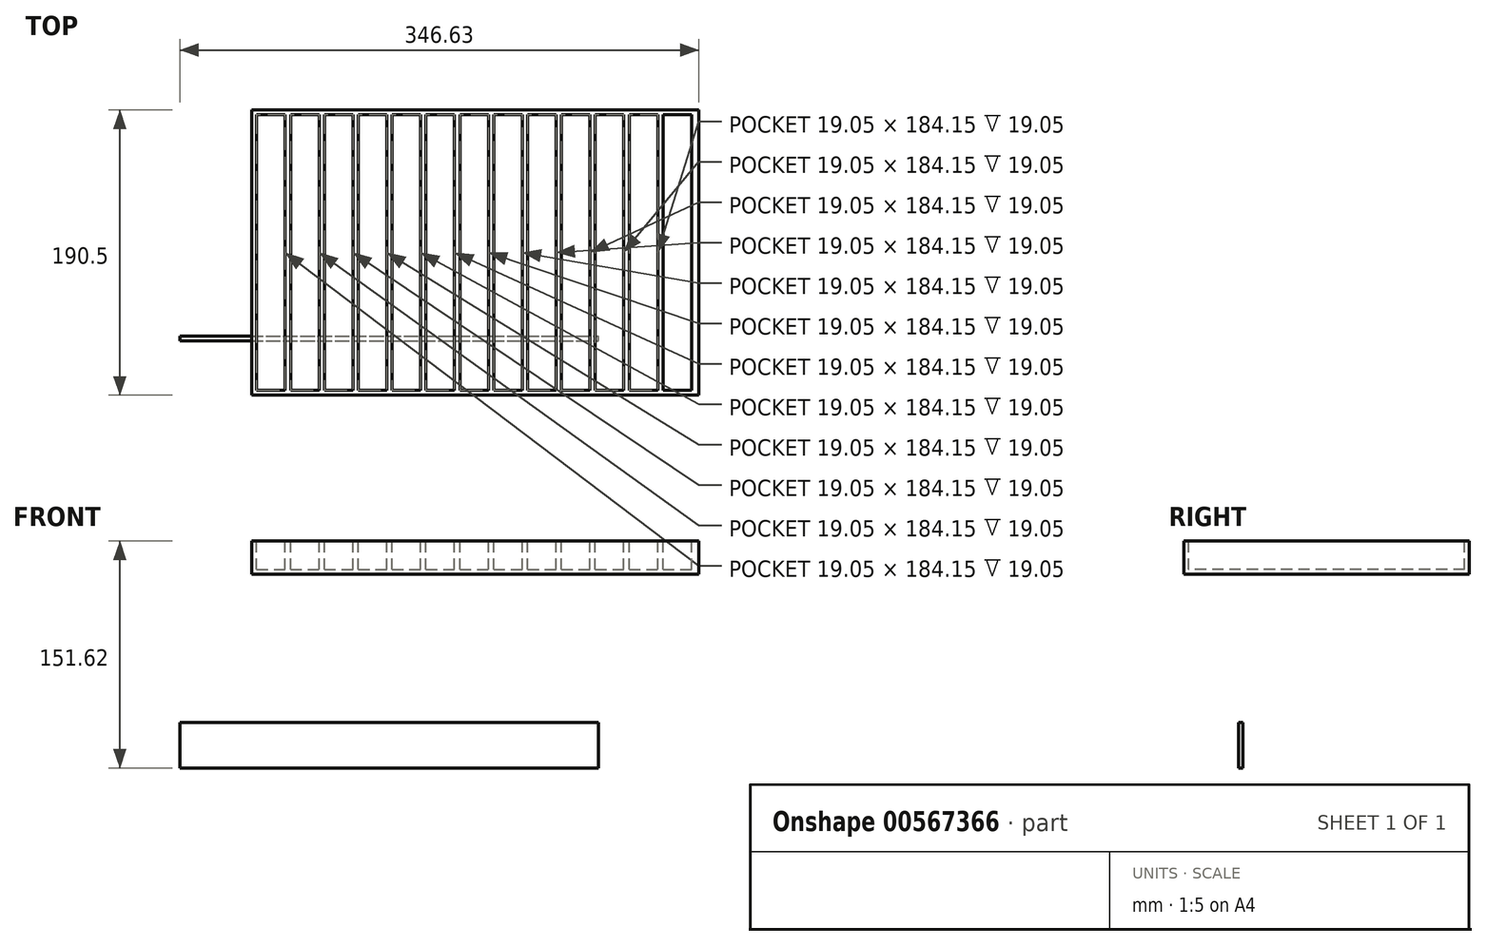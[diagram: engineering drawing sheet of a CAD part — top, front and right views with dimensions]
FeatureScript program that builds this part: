
annotation { "Feature Type Name" : "Feature", "Feature Type Description" : "" }
export const myFeature = defineFeature(function(context is Context, id is Id, definition is map)
    precondition{}
    {
        {
            var Q0;
            Q0=qCreatedBy(makeId("Top.planeOp"),FACE);
            var sketch = newSketch(context, id + "F0", { "sketchPlane" : qUnion([Q0])});
            skLineSegment(sketch, "E0.bottom", {"start": v(-114.24, 151.05) * mm, "end": v(184.2, 151.05) * mm});
            skLineSegment(sketch, "E0.top", {"start": v(-114.24, -39.45) * mm, "end": v(184.2, -39.45) * mm});
            skLineSegment(sketch, "E0.left", {"start": v(-114.24, 151.05) * mm, "end": v(-114.24, -39.45) * mm});
            skLineSegment(sketch, "E0.right", {"start": v(184.2, 151.05) * mm, "end": v(184.2, -39.45) * mm});
            skSolve(sketch);
        }
        {
            var Q0;
            Q0=makeQuery(id+"F0.imprint","IMPRINT",FACE,{"disambiguationData":[TD([[makeQuery(id+"F0.imprint","IMPRINT",EDGE,{"derivedFrom":sQuery(id+"F0.wireOp",EDGE,"E0.bottom")}),-1.0]])]});
            extrude(context, id + "F1", {"entities" : qUnion([Q0]), "depth" : 22.22 * mm, "offsetDistance" : 25.4 * mm});
        }
        {
            var Q0;
            Q0=qCreatedBy(makeId("Front.planeOp"),FACE);
            var sketch = newSketch(context, id + "F2", { "sketchPlane" : qUnion([Q0])});
            skLineSegment(sketch, "E1.bottom", {"start": v(-162.42, -98.91) * mm, "end": v(116.98, -98.91) * mm});
            skLineSegment(sketch, "E1.top", {"start": v(-162.42, -129.4) * mm, "end": v(116.98, -129.4) * mm});
            skLineSegment(sketch, "E1.left", {"start": v(-162.42, -98.91) * mm, "end": v(-162.42, -129.4) * mm});
            skLineSegment(sketch, "E1.right", {"start": v(116.98, -98.91) * mm, "end": v(116.98, -129.4) * mm});
            skSolve(sketch);
        }
        {
            var Q0;
            Q0=makeQuery(id+"F2.imprint","IMPRINT",FACE,{"disambiguationData":[TD([[makeQuery(id+"F2.imprint","IMPRINT",EDGE,{"derivedFrom":sQuery(id+"F2.wireOp",EDGE,"E1.bottom")}),-1.0]])]});
            extrude(context, id + "F3", {"entities" : qUnion([Q0]), "depth" : 3.17 * mm, "offsetDistance" : 25.4 * mm});
        }
        {
            var Q0;
            Q0=makeQuery(id+"F1.opExtrude","CAP_FACE",FACE,{"disambiguationData":[OSD([sQuery(id+"F0.wireOp",EDGE,"E0.bottom"),sQuery(id+"F0.wireOp",EDGE,"E0.top"),sQuery(id+"F0.wireOp",EDGE,"E0.left"),sQuery(id+"F0.wireOp",EDGE,"E0.right")])],"isStart":false});
            var sketch = newSketch(context, id + "F4", { "sketchPlane" : qUnion([Q0])});
            skLineSegment(sketch, "E2.bottom", {"start": v(-111.07, 147.87) * mm, "end": v(-92.02, 147.87) * mm});
            skLineSegment(sketch, "E2.top", {"start": v(-111.07, -36.28) * mm, "end": v(-92.02, -36.28) * mm});
            skLineSegment(sketch, "E2.left", {"start": v(-111.07, 147.87) * mm, "end": v(-111.07, -36.28) * mm});
            skLineSegment(sketch, "E2.right", {"start": v(-92.02, 147.87) * mm, "end": v(-92.02, -36.28) * mm});
            skLineSegment(sketch, "E3.1.0.0", {"start": v(-88.46, 147.87) * mm, "end": v(-88.46, -36.28) * mm});
            skLineSegment(sketch, "E3.1.0.1", {"start": v(-69.41, 147.87) * mm, "end": v(-69.41, -36.28) * mm});
            skLineSegment(sketch, "E3.1.0.2", {"start": v(-88.46, 147.87) * mm, "end": v(-69.41, 147.87) * mm});
            skLineSegment(sketch, "E3.1.0.3", {"start": v(-88.46, -36.28) * mm, "end": v(-69.41, -36.28) * mm});
            skLineSegment(sketch, "E3.2.0.0", {"start": v(-65.86, 147.87) * mm, "end": v(-65.86, -36.28) * mm});
            skLineSegment(sketch, "E3.2.0.1", {"start": v(-46.8, 147.87) * mm, "end": v(-46.8, -36.28) * mm});
            skLineSegment(sketch, "E3.2.0.2", {"start": v(-65.86, 147.87) * mm, "end": v(-46.8, 147.87) * mm});
            skLineSegment(sketch, "E3.2.0.3", {"start": v(-65.86, -36.28) * mm, "end": v(-46.8, -36.28) * mm});
            skLineSegment(sketch, "E3.3.0.0", {"start": v(-43.25, 147.87) * mm, "end": v(-43.25, -36.28) * mm});
            skLineSegment(sketch, "E3.3.0.1", {"start": v(-24.2, 147.87) * mm, "end": v(-24.2, -36.28) * mm});
            skLineSegment(sketch, "E3.3.0.2", {"start": v(-43.25, 147.87) * mm, "end": v(-24.2, 147.87) * mm});
            skLineSegment(sketch, "E3.3.0.3", {"start": v(-43.25, -36.28) * mm, "end": v(-24.2, -36.28) * mm});
            skLineSegment(sketch, "E3.4.0.0", {"start": v(-20.65, 147.87) * mm, "end": v(-20.65, -36.28) * mm});
            skLineSegment(sketch, "E3.4.0.1", {"start": v(-1.6, 147.87) * mm, "end": v(-1.6, -36.28) * mm});
            skLineSegment(sketch, "E3.4.0.2", {"start": v(-20.65, 147.87) * mm, "end": v(-1.6, 147.87) * mm});
            skLineSegment(sketch, "E3.4.0.3", {"start": v(-20.65, -36.28) * mm, "end": v(-1.6, -36.28) * mm});
            skLineSegment(sketch, "E3.5.0.0", {"start": v(1.96, 147.87) * mm, "end": v(1.96, -36.28) * mm});
            skLineSegment(sketch, "E3.5.0.1", {"start": v(21.01, 147.87) * mm, "end": v(21.01, -36.28) * mm});
            skLineSegment(sketch, "E3.5.0.2", {"start": v(1.96, 147.87) * mm, "end": v(21.01, 147.87) * mm});
            skLineSegment(sketch, "E3.5.0.3", {"start": v(1.96, -36.28) * mm, "end": v(21.01, -36.28) * mm});
            skLineSegment(sketch, "E3.6.0.0", {"start": v(24.57, 147.87) * mm, "end": v(24.57, -36.28) * mm});
            skLineSegment(sketch, "E3.6.0.1", {"start": v(43.62, 147.87) * mm, "end": v(43.62, -36.28) * mm});
            skLineSegment(sketch, "E3.6.0.2", {"start": v(24.57, 147.87) * mm, "end": v(43.62, 147.87) * mm});
            skLineSegment(sketch, "E3.6.0.3", {"start": v(24.57, -36.28) * mm, "end": v(43.62, -36.28) * mm});
            skLineSegment(sketch, "E3.7.0.0", {"start": v(47.17, 147.87) * mm, "end": v(47.17, -36.28) * mm});
            skLineSegment(sketch, "E3.7.0.1", {"start": v(66.22, 147.87) * mm, "end": v(66.22, -36.28) * mm});
            skLineSegment(sketch, "E3.7.0.2", {"start": v(47.17, 147.87) * mm, "end": v(66.22, 147.87) * mm});
            skLineSegment(sketch, "E3.7.0.3", {"start": v(47.17, -36.28) * mm, "end": v(66.22, -36.28) * mm});
            skLineSegment(sketch, "E3.8.0.0", {"start": v(69.78, 147.87) * mm, "end": v(69.78, -36.28) * mm});
            skLineSegment(sketch, "E3.8.0.1", {"start": v(88.83, 147.87) * mm, "end": v(88.83, -36.28) * mm});
            skLineSegment(sketch, "E3.8.0.2", {"start": v(69.78, 147.87) * mm, "end": v(88.83, 147.87) * mm});
            skLineSegment(sketch, "E3.8.0.3", {"start": v(69.78, -36.28) * mm, "end": v(88.83, -36.28) * mm});
            skLineSegment(sketch, "E3.9.0.0", {"start": v(92.38, 147.87) * mm, "end": v(92.38, -36.28) * mm});
            skLineSegment(sketch, "E3.9.0.1", {"start": v(111.43, 147.87) * mm, "end": v(111.43, -36.28) * mm});
            skLineSegment(sketch, "E3.9.0.2", {"start": v(92.38, 147.87) * mm, "end": v(111.43, 147.87) * mm});
            skLineSegment(sketch, "E3.9.0.3", {"start": v(92.38, -36.28) * mm, "end": v(111.43, -36.28) * mm});
            skLineSegment(sketch, "E3.10.0.0", {"start": v(115, 147.87) * mm, "end": v(115, -36.28) * mm});
            skLineSegment(sketch, "E3.10.0.1", {"start": v(134.04, 147.87) * mm, "end": v(134.04, -36.28) * mm});
            skLineSegment(sketch, "E3.10.0.2", {"start": v(115, 147.87) * mm, "end": v(134.04, 147.87) * mm});
            skLineSegment(sketch, "E3.10.0.3", {"start": v(115, -36.28) * mm, "end": v(134.04, -36.28) * mm});
            skLineSegment(sketch, "E3.direction1", {"start": v(-111.07, -36.28) * mm, "end": v(-88.46, -36.28) * mm, "construction": true});
            skLineSegment(sketch, "E4.0.11.0", {"start": v(137.6, 147.87) * mm, "end": v(137.6, -36.28) * mm});
            skLineSegment(sketch, "E4.3.11.0", {"start": v(156.65, 147.87) * mm, "end": v(156.65, -36.28) * mm});
            skLineSegment(sketch, "E4.6.11.0", {"start": v(137.6, 147.87) * mm, "end": v(156.65, 147.87) * mm});
            skLineSegment(sketch, "E4.9.11.0", {"start": v(137.6, -36.28) * mm, "end": v(156.65, -36.28) * mm});
            skLineSegment(sketch, "E5.0.12.0", {"start": v(160.2, 147.87) * mm, "end": v(160.2, -36.28) * mm});
            skLineSegment(sketch, "E5.3.12.0", {"start": v(179.25, 147.87) * mm, "end": v(179.25, -36.28) * mm});
            skLineSegment(sketch, "E5.6.12.0", {"start": v(160.2, 147.87) * mm, "end": v(179.25, 147.87) * mm});
            skLineSegment(sketch, "E5.9.12.0", {"start": v(160.2, -36.28) * mm, "end": v(179.25, -36.28) * mm});
            skSolve(sketch);
        }
        {
            var Q0;
            Q0=makeQuery(id+"F4.imprint","IMPRINT",FACE,{"disambiguationData":[TD([[makeQuery(id+"F4.imprint","IMPRINT",EDGE,{"derivedFrom":sQuery(id+"F4.wireOp",EDGE,"E2.bottom")}),-1.0]])]});
            var Q1;
            Q1=makeQuery(id+"F4.imprint","IMPRINT",FACE,{"disambiguationData":[TD([[makeQuery(id+"F4.imprint","IMPRINT",EDGE,{"derivedFrom":sQuery(id+"F4.wireOp",EDGE,"E3.1.0.0")}),1.0]])]});
            var Q2;
            Q2=makeQuery(id+"F4.imprint","IMPRINT",FACE,{"disambiguationData":[TD([[makeQuery(id+"F4.imprint","IMPRINT",EDGE,{"derivedFrom":sQuery(id+"F4.wireOp",EDGE,"E3.2.0.0")}),1.0]])]});
            var Q3;
            Q3=makeQuery(id+"F4.imprint","IMPRINT",FACE,{"disambiguationData":[TD([[makeQuery(id+"F4.imprint","IMPRINT",EDGE,{"derivedFrom":sQuery(id+"F4.wireOp",EDGE,"E3.3.0.0")}),1.0]])]});
            var Q4;
            Q4=makeQuery(id+"F4.imprint","IMPRINT",FACE,{"disambiguationData":[TD([[makeQuery(id+"F4.imprint","IMPRINT",EDGE,{"derivedFrom":sQuery(id+"F4.wireOp",EDGE,"E3.4.0.0")}),1.0]])]});
            var Q5;
            Q5=makeQuery(id+"F4.imprint","IMPRINT",FACE,{"disambiguationData":[TD([[makeQuery(id+"F4.imprint","IMPRINT",EDGE,{"derivedFrom":sQuery(id+"F4.wireOp",EDGE,"E3.5.0.0")}),1.0]])]});
            var Q6;
            Q6=makeQuery(id+"F4.imprint","IMPRINT",FACE,{"disambiguationData":[TD([[makeQuery(id+"F4.imprint","IMPRINT",EDGE,{"derivedFrom":sQuery(id+"F4.wireOp",EDGE,"E3.6.0.0")}),1.0]])]});
            var Q7;
            Q7=makeQuery(id+"F4.imprint","IMPRINT",FACE,{"disambiguationData":[TD([[makeQuery(id+"F4.imprint","IMPRINT",EDGE,{"derivedFrom":sQuery(id+"F4.wireOp",EDGE,"E3.7.0.0")}),1.0]])]});
            var Q8;
            Q8=makeQuery(id+"F4.imprint","IMPRINT",FACE,{"disambiguationData":[TD([[makeQuery(id+"F4.imprint","IMPRINT",EDGE,{"derivedFrom":sQuery(id+"F4.wireOp",EDGE,"E3.8.0.0")}),1.0]])]});
            var Q9;
            Q9=makeQuery(id+"F4.imprint","IMPRINT",FACE,{"disambiguationData":[TD([[makeQuery(id+"F4.imprint","IMPRINT",EDGE,{"derivedFrom":sQuery(id+"F4.wireOp",EDGE,"E3.9.0.0")}),1.0]])]});
            var Q10;
            Q10=makeQuery(id+"F4.imprint","IMPRINT",FACE,{"disambiguationData":[TD([[makeQuery(id+"F4.imprint","IMPRINT",EDGE,{"derivedFrom":sQuery(id+"F4.wireOp",EDGE,"E3.10.0.0")}),1.0]])]});
            var Q11;
            Q11=makeQuery(id+"F4.imprint","IMPRINT",FACE,{"disambiguationData":[TD([[makeQuery(id+"F4.imprint","IMPRINT",EDGE,{"derivedFrom":sQuery(id+"F4.wireOp",EDGE,"E4.0.11.0")}),1.0]])]});
            var Q12;
            Q12=makeQuery(id+"F4.imprint","IMPRINT",FACE,{"disambiguationData":[TD([[makeQuery(id+"F4.imprint","IMPRINT",EDGE,{"derivedFrom":sQuery(id+"F4.wireOp",EDGE,"E5.0.12.0")}),1.0]])]});
            extrude(context, id + "F5", {"entities" : qUnion([Q0, Q1, Q2, Q3, Q4, Q5, Q6, Q7, Q8, Q9, Q10, Q11, Q12]), "operationType" : NewBodyOperationType.REMOVE, "oppositeDirection" : true, "depth" : 19.05 * mm, "offsetDistance" : 25.4 * mm});
        }
    });
